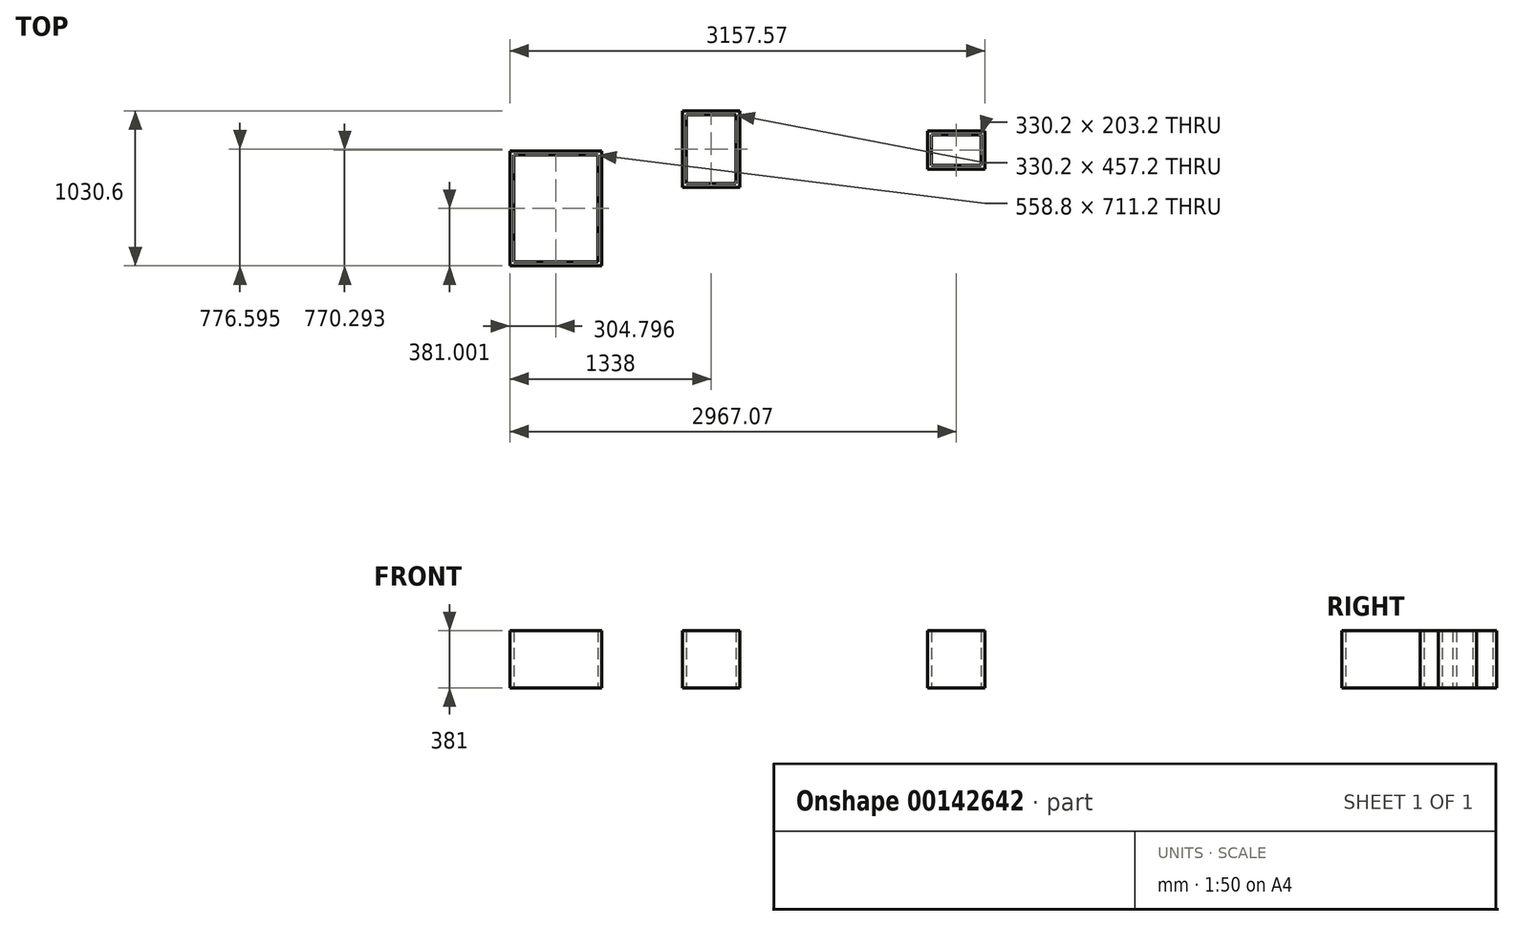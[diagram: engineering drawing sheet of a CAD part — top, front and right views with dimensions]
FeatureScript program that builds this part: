
annotation { "Feature Type Name" : "Feature", "Feature Type Description" : "" }
export const myFeature = defineFeature(function(context is Context, id is Id, definition is map)
    precondition{}
    {
        {
            var Q0;
            Q0=qCreatedBy(makeId("Top.planeOp"),FACE);
            var sketch = newSketch(context, id + "F0", { "sketchPlane" : qUnion([Q0])});
            skLineSegment(sketch, "E0.bottom", {"start": v(-315.91, 356.94) * mm, "end": v(293.69, 356.94) * mm});
            skLineSegment(sketch, "E0.top", {"start": v(-315.91, -405.06) * mm, "end": v(293.69, -405.06) * mm});
            skLineSegment(sketch, "E0.left", {"start": v(-315.91, 356.94) * mm, "end": v(-315.91, -405.06) * mm});
            skLineSegment(sketch, "E0.right", {"start": v(293.69, 356.94) * mm, "end": v(293.69, -405.06) * mm});
            skLineSegment(sketch, "E1.0", {"start": v(-290.51, 331.54) * mm, "end": v(268.29, 331.54) * mm});
            skLineSegment(sketch, "E1.1", {"start": v(-290.51, 331.54) * mm, "end": v(-290.51, -379.66) * mm});
            skLineSegment(sketch, "E1.2", {"start": v(-290.51, -379.66) * mm, "end": v(268.29, -379.66) * mm});
            skLineSegment(sketch, "E1.3", {"start": v(268.29, 331.54) * mm, "end": v(268.29, -379.66) * mm});
            skSolve(sketch);
        }
        {
            var Q0;
            Q0=makeQuery(id+"F0.imprint","IMPRINT",FACE,{"disambiguationData":[TD([[makeQuery(id+"F0.imprint","IMPRINT",EDGE,{"derivedFrom":sQuery(id+"F0.wireOp",EDGE,"E0.bottom")}),-1.0]])]});
            extrude(context, id + "F1", {"entities" : qUnion([Q0]), "depth" : 381 * mm});
        }
        {
            var Q0;
            Q0=qCreatedBy(makeId("Top.planeOp"),FACE);
            var sketch = newSketch(context, id + "F2", { "sketchPlane" : qUnion([Q0])});
            skLineSegment(sketch, "E2.bottom", {"start": v(831.6, 625.54) * mm, "end": v(1212.6, 625.54) * mm});
            skLineSegment(sketch, "E2.top", {"start": v(831.6, 117.54) * mm, "end": v(1212.6, 117.54) * mm});
            skLineSegment(sketch, "E2.left", {"start": v(831.6, 625.54) * mm, "end": v(831.6, 117.54) * mm});
            skLineSegment(sketch, "E2.right", {"start": v(1212.6, 625.54) * mm, "end": v(1212.6, 117.54) * mm});
            skLineSegment(sketch, "E3.0", {"start": v(857, 600.14) * mm, "end": v(1187.2, 600.14) * mm});
            skLineSegment(sketch, "E3.1", {"start": v(857, 600.14) * mm, "end": v(857, 142.94) * mm});
            skLineSegment(sketch, "E3.2", {"start": v(857, 142.94) * mm, "end": v(1187.2, 142.94) * mm});
            skLineSegment(sketch, "E3.3", {"start": v(1187.2, 600.14) * mm, "end": v(1187.2, 142.94) * mm});
            skSolve(sketch);
        }
        {
            var Q0;
            Q0 = qSketchRegion(id + "F2", true);
            extrude(context, id + "F3", {"entities" : qUnion([Q0]), "depth" : 381 * mm});
        }
        {
            var Q0;
            Q0=qCreatedBy(makeId("Top.planeOp"),FACE);
            var sketch = newSketch(context, id + "F4", { "sketchPlane" : qUnion([Q0])});
            skLineSegment(sketch, "E4.bottom", {"start": v(2486.06, 466.83) * mm, "end": v(2816.26, 466.83) * mm});
            skLineSegment(sketch, "E4.top", {"start": v(2486.06, 263.63) * mm, "end": v(2816.26, 263.63) * mm});
            skLineSegment(sketch, "E4.left", {"start": v(2486.06, 466.83) * mm, "end": v(2486.06, 263.63) * mm});
            skLineSegment(sketch, "E4.right", {"start": v(2816.26, 466.83) * mm, "end": v(2816.26, 263.63) * mm});
            skLineSegment(sketch, "E5.0", {"start": v(2460.66, 492.23) * mm, "end": v(2460.66, 238.23) * mm});
            skLineSegment(sketch, "E5.1", {"start": v(2460.66, 492.23) * mm, "end": v(2841.66, 492.23) * mm});
            skLineSegment(sketch, "E5.2", {"start": v(2841.66, 492.23) * mm, "end": v(2841.66, 238.23) * mm});
            skLineSegment(sketch, "E5.3", {"start": v(2460.66, 238.23) * mm, "end": v(2841.66, 238.23) * mm});
            skSolve(sketch);
        }
        {
            var Q0;
            Q0=makeQuery(id+"F4.imprint","IMPRINT",FACE,{"disambiguationData":[TD([[makeQuery(id+"F4.imprint","IMPRINT",EDGE,{"derivedFrom":sQuery(id+"F4.wireOp",EDGE,"E4.bottom")}),1.0]])]});
            extrude(context, id + "F5", {"entities" : qUnion([Q0]), "depth" : 381 * mm});
        }
    });
